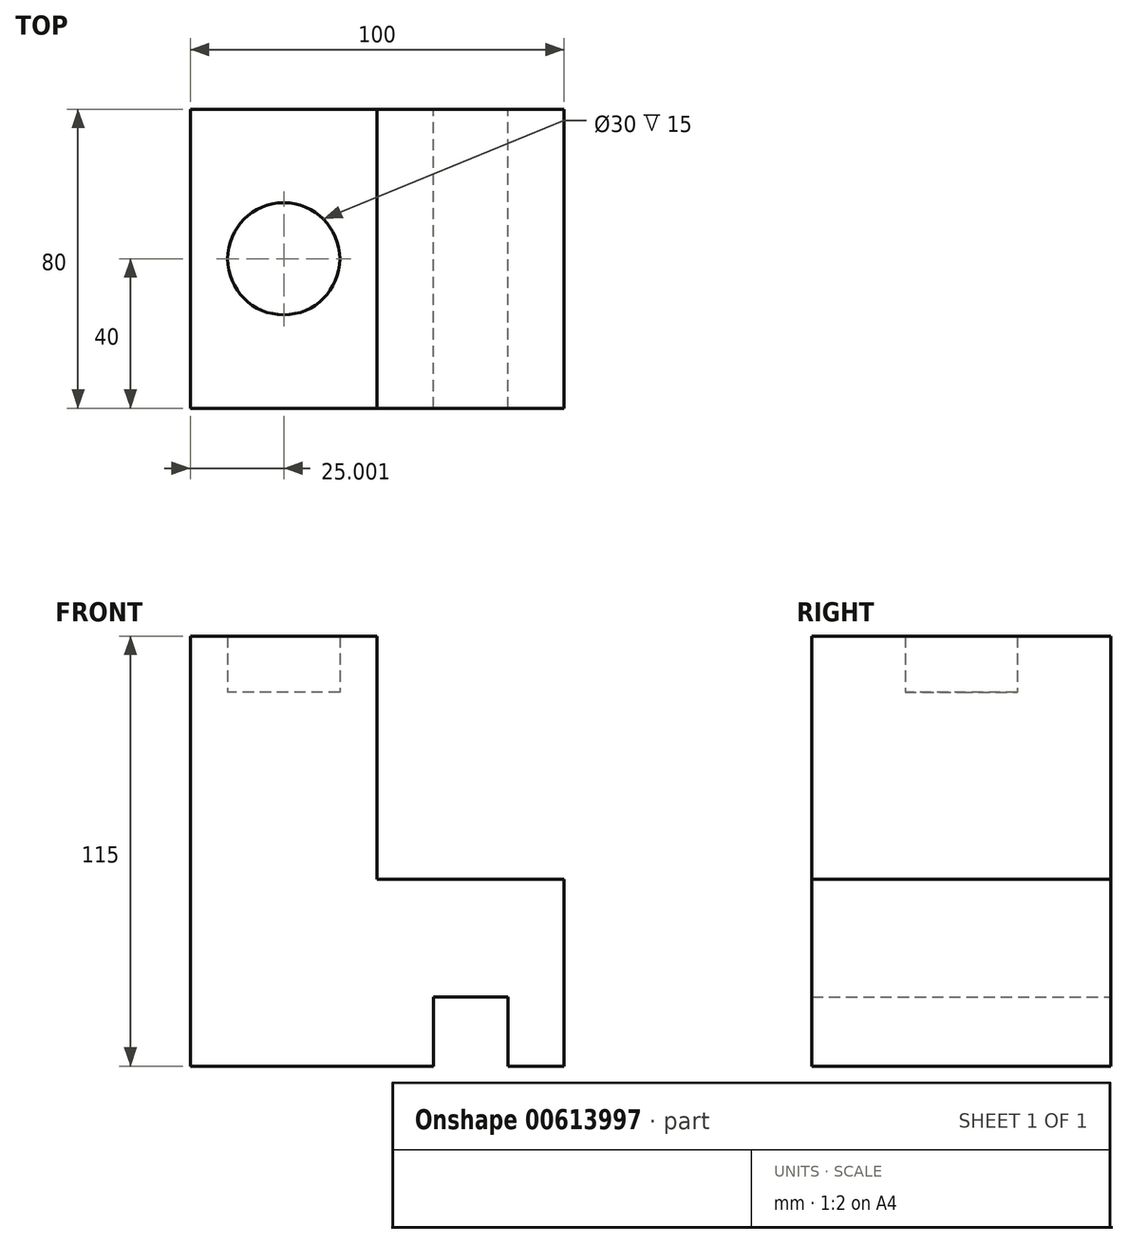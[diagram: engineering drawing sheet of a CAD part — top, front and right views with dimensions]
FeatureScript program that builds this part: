
annotation { "Feature Type Name" : "Feature", "Feature Type Description" : "" }
export const myFeature = defineFeature(function(context is Context, id is Id, definition is map)
    precondition{}
    {
        {
            var Q0;
            Q0=qCreatedBy(makeId("Front.planeOp"),FACE);
            var sketch = newSketch(context, id + "F0", { "sketchPlane" : qUnion([Q0])});
            skLineSegment(sketch, "E0", {"start": v(-42.74, 50) * mm, "end": v(-42.74, -50) * mm});
            skLineSegment(sketch, "E1", {"start": v(-42.74, -50) * mm, "end": v(22.26, -50) * mm});
            skLineSegment(sketch, "E2", {"start": v(57.26, -50) * mm, "end": v(57.26, 0) * mm});
            skLineSegment(sketch, "E3", {"start": v(-42.74, 50) * mm, "end": v(7.26, 50) * mm});
            skLineSegment(sketch, "E4", {"start": v(57.26, 0) * mm, "end": v(7.26, 0) * mm});
            skLineSegment(sketch, "E5", {"start": v(7.26, 0) * mm, "end": v(7.26, 50) * mm});
            skLineSegment(sketch, "E6", {"start": v(22.26, -31.53) * mm, "end": v(22.26, -50) * mm});
            skLineSegment(sketch, "E7", {"start": v(42.26, -31.53) * mm, "end": v(42.26, -50) * mm});
            skLineSegment(sketch, "E8", {"start": v(42.26, -31.53) * mm, "end": v(22.26, -31.53) * mm});
            skPoint(sketch, "E8.endSnap0", {"position": v(22.26, -40.72) * mm});
            skPoint(sketch, "E9.orphan", {"position": v(22.26, -31.45) * mm});
            skLineSegment(sketch, "E10.trimOffspring", {"start": v(42.26, -50) * mm, "end": v(57.26, -50) * mm});
            skSolve(sketch);
        }
        {
            var Q0;
            Q0=makeQuery(id+"F0.imprint","IMPRINT",FACE,{"disambiguationData":[TD([[makeQuery(id+"F0.imprint","IMPRINT",EDGE,{"derivedFrom":sQuery(id+"F0.wireOp",EDGE,"E0")}),1.0]])]});
            extrude(context, id + "F1", {"entities" : qUnion([Q0]), "depth" : 80 * mm, "offsetDistance" : 25 * mm});
        }
        {
            var Q0;
            Q0=makeQuery(id+"F1.opExtrude","SWEPT_FACE",FACE,{"disambiguationData":[OSD([sQuery(id+"F0.wireOp",EDGE,"E3")])]});
            var sketch = newSketch(context, id + "F2", { "sketchPlane" : qUnion([Q0])});
            skCircle(sketch, "E11", {"center": v(-17.74, -40) * mm, "radius": 15 * mm});
            skPoint(sketch, "E12.orphan", {"position": v(-17.74, 0) * mm});
            skPoint(sketch, "E13.orphan", {"position": v(-42.74, -40) * mm});
            skPoint(sketch, "E14.start.orphan", {"position": v(7.26, -40) * mm});
            skPoint(sketch, "E15.orphan", {"position": v(-17.74, -80) * mm});
            skLineSegment(sketch, "E16", {"start": v(-42.74, 0) * mm, "end": v(-42.74, -80) * mm});
            skLineSegment(sketch, "E17", {"start": v(-42.74, -80) * mm, "end": v(7.26, -80) * mm});
            skLineSegment(sketch, "E18", {"start": v(7.26, -80) * mm, "end": v(7.26, 0) * mm});
            skLineSegment(sketch, "E19", {"start": v(7.26, 0) * mm, "end": v(-42.74, 0) * mm});
            skSolve(sketch);
        }
        {
            var Q0;
            Q0 = qSketchRegion(id + "F2", true);
            extrude(context, id + "F3", {"entities" : qUnion([Q0]), "operationType" : NewBodyOperationType.ADD, "depth" : 15 * mm, "offsetDistance" : 25 * mm});
        }
    });
